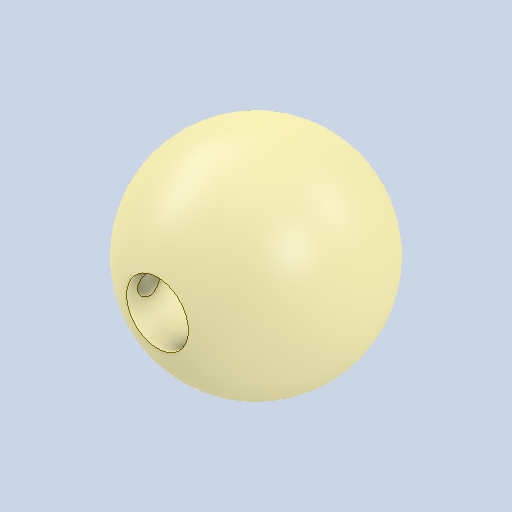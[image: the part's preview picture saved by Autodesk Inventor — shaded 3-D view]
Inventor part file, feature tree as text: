
AUTODESK INVENTOR PART (.ipt)
format: ipt  version: 2025.2 (Build 292293000, 293)  size: 401,920 bytes
history: native  units: mm
features: other x3, sketch x3, extrude x1
ambient origin geometry x8: Origin, YZ Plane, XZ Plane, XY Plane, X Axis, Y Axis, Z Axis, Center Point
bodies: Body1 (feature_tree)
feature tree (7):
  other  "Sólido1"
  other  "Revolução1"
  other  "Revolução2"
  extrude  "Extrusão1"  Depth=3.0mm
  sketch  "Esboço1"  dims[d0=10.0mm d2=3.0mm]
  sketch  "Esboço2"  dims[d3=360.0deg]
  sketch  "Esboço4"  dims[d4=1.0mm d5=4.0mm d6=10.0mm d7=360.0deg d10=3.0mm d11=10.0mm d12=0.0mm]
